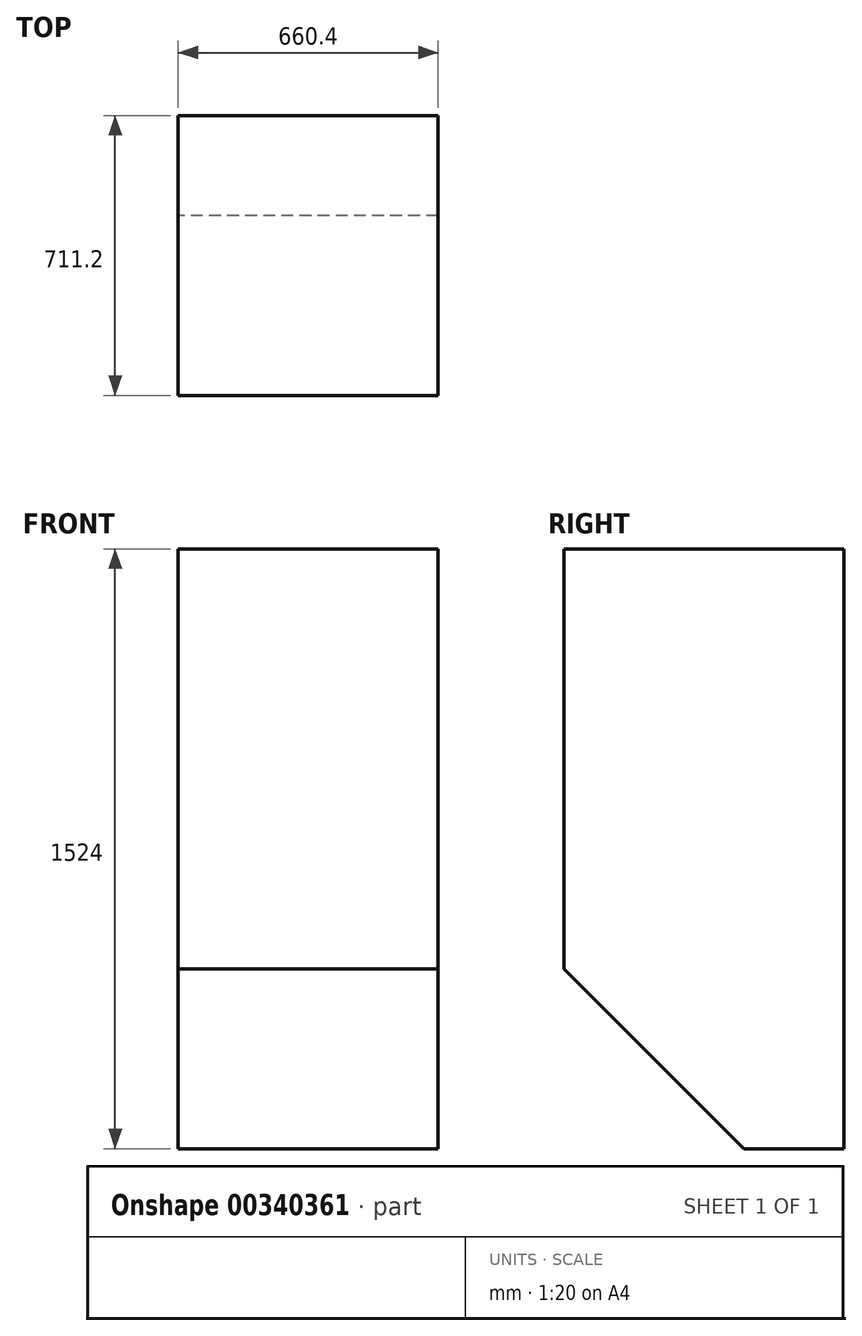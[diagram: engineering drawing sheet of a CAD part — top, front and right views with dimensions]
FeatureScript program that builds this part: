
annotation { "Feature Type Name" : "Feature", "Feature Type Description" : "" }
export const myFeature = defineFeature(function(context is Context, id is Id, definition is map)
    precondition{}
    {
        {
            var Q0;
            Q0=qCreatedBy(makeId("Front.planeOp"),FACE);
            var sketch = newSketch(context, id + "F0", { "sketchPlane" : qUnion([Q0])});
            skLineSegment(sketch, "E0.bottom", {"start": v(-330.2, 762) * mm, "end": v(330.2, 762) * mm});
            skLineSegment(sketch, "E0.top", {"start": v(-330.2, -762) * mm, "end": v(330.2, -762) * mm});
            skLineSegment(sketch, "E0.left", {"start": v(-330.2, 762) * mm, "end": v(-330.2, -762) * mm});
            skLineSegment(sketch, "E0.right", {"start": v(330.2, 762) * mm, "end": v(330.2, -762) * mm});
            skPoint(sketch, "E0.middle", {"position": v(0, 0) * mm});
            skSolve(sketch);
        }
        {
            var Q0;
            Q0 = qSketchRegion(id + "F0", true);
            extrude(context, id + "F1", {"entities" : qUnion([Q0]), "depth" : 711.2 * mm});
        }
        {
            var Q0;
            Q0=makeQuery(id+"F1.opExtrude","CAP_EDGE",EDGE,{"disambiguationData":[OSD([sQuery(id+"F0.wireOp",EDGE,"E0.top")])],"isStart":false});
            chamfer(context, id + "F2", {"entities" : qUnion([Q0]), "width" : 457.2 * mm, "tangentPropagation" : true});
        }
    });
